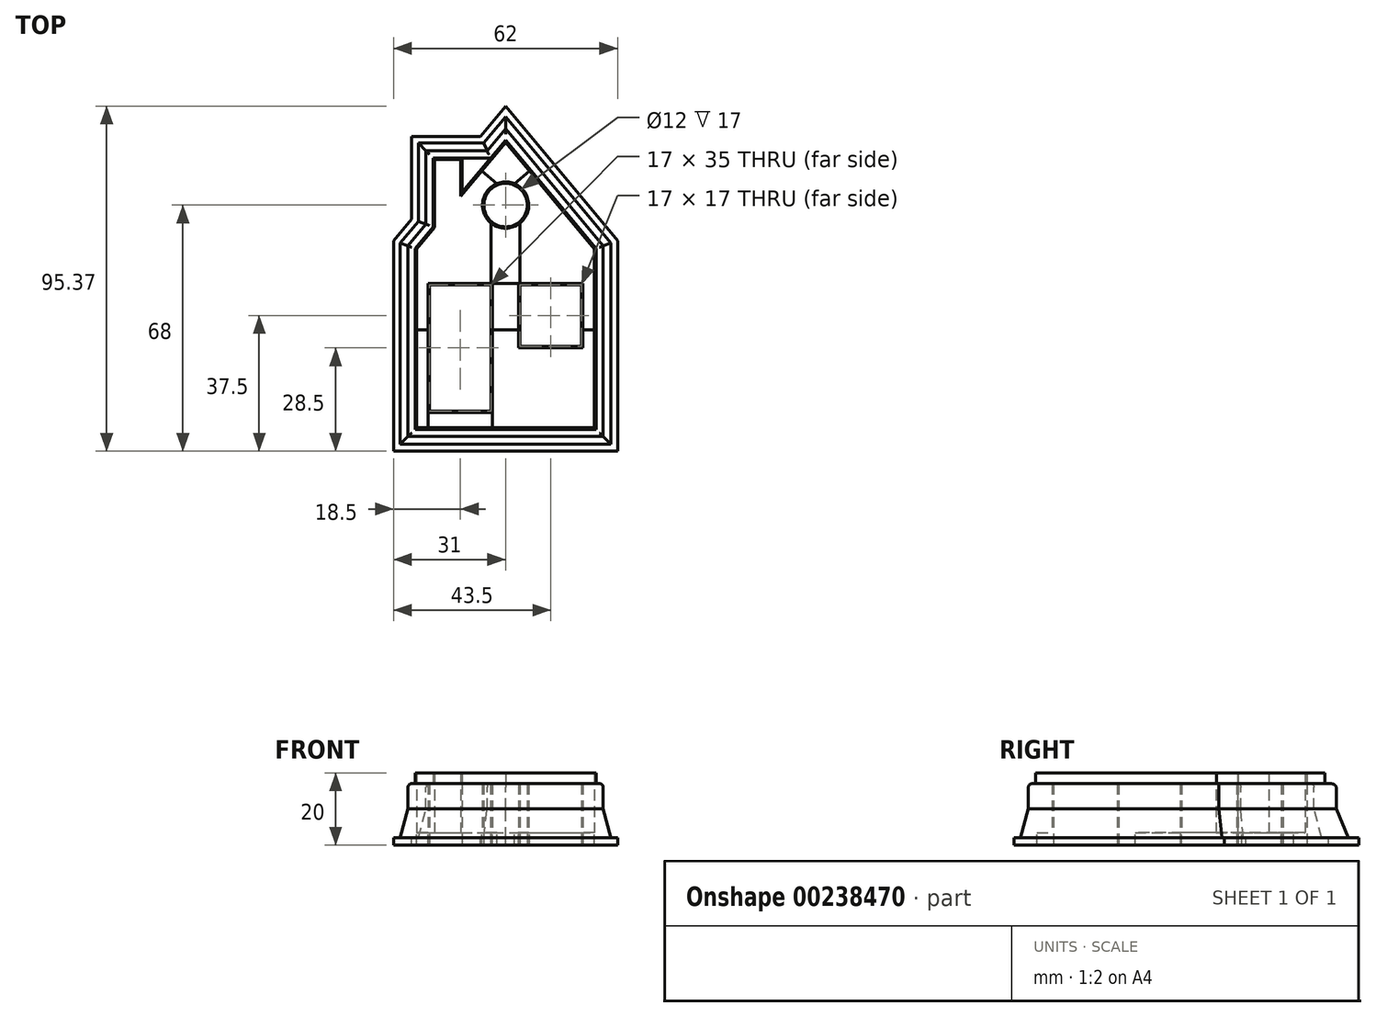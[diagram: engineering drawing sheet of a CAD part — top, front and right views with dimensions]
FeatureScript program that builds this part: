
annotation { "Feature Type Name" : "Feature", "Feature Type Description" : "" }
export const myFeature = defineFeature(function(context is Context, id is Id, definition is map)
    precondition{}
    {
        {
            var Q0;
            Q0=qCreatedBy(makeId("Top.planeOp"),FACE);
            var sketch = newSketch(context, id + "F0", { "sketchPlane" : qUnion([Q0])});
            skLineSegment(sketch, "E0.bottom", {"start": v(-25, 50) * mm, "end": v(25, 50) * mm});
            skLineSegment(sketch, "E0.top", {"start": v(-25, 0) * mm, "end": v(25, 0) * mm});
            skLineSegment(sketch, "E0.left", {"start": v(-25, 50) * mm, "end": v(-25, 0) * mm});
            skLineSegment(sketch, "E0.right", {"start": v(25, 50) * mm, "end": v(25, 0) * mm});
            skPoint(sketch, "E0.middle", {"position": v(0, 25) * mm});
            skLineSegment(sketch, "E1", {"start": v(-25, 50) * mm, "end": v(-20, 56) * mm});
            skLineSegment(sketch, "E2", {"start": v(0, 80) * mm, "end": v(25, 50) * mm});
            skLineSegment(sketch, "E3.bottom", {"start": v(-21, 5) * mm, "end": v(-4, 5) * mm});
            skLineSegment(sketch, "E3.top", {"start": v(-21, 40) * mm, "end": v(-4, 40) * mm});
            skLineSegment(sketch, "E3.left", {"start": v(-21, 5) * mm, "end": v(-21, 40) * mm});
            skLineSegment(sketch, "E3.right", {"start": v(-4, 5) * mm, "end": v(-4, 40) * mm});
            skLineSegment(sketch, "E4.bottom", {"start": v(4, 40) * mm, "end": v(21, 40) * mm});
            skLineSegment(sketch, "E4.top", {"start": v(4, 23) * mm, "end": v(21, 23) * mm});
            skLineSegment(sketch, "E4.left", {"start": v(4, 40) * mm, "end": v(4, 23) * mm});
            skLineSegment(sketch, "E4.right", {"start": v(21, 40) * mm, "end": v(21, 23) * mm});
            skLineSegment(sketch, "E5", {"start": v(-25, 40) * mm, "end": v(25, 40) * mm, "construction": true});
            skCircle(sketch, "E6", {"center": v(0, 62) * mm, "radius": 6 * mm});
            skLineSegment(sketch, "E7", {"start": v(-20, 56) * mm, "end": v(-20, 75) * mm});
            skLineSegment(sketch, "E8", {"start": v(-20, 75) * mm, "end": v(-12, 75) * mm});
            skLineSegment(sketch, "E9", {"start": v(-12, 75) * mm, "end": v(-12, 65.6) * mm});
            skLineSegment(sketch, "E10.trimOffspring", {"start": v(-12, 65.6) * mm, "end": v(0, 80) * mm});
            skSolve(sketch);
        }
        {
            var Q0;
            Q0=makeQuery(id+"F0.imprint","IMPRINT",FACE,{"disambiguationData":[TD([[makeQuery(id+"F0.imprint","IMPRINT",EDGE,{"derivedFrom":sQuery(id+"F0.wireOp",EDGE,"E0.bottom")}),1.0]])]});
            var Q1;
            Q1=makeQuery(id+"F0.imprint","IMPRINT",FACE,{"disambiguationData":[TD([[makeQuery(id+"F0.imprint","IMPRINT",EDGE,{"derivedFrom":sQuery(id+"F0.wireOp",EDGE,"E0.bottom")}),-1.0]])]});
            extrude(context, id + "F1", {"entities" : qUnion([Q0, Q1]), "depth" : 20 * mm});
        }
        {
            var Q0;
            Q0=makeQuery(id+"F1.opExtrude","CAP_FACE",FACE,{"disambiguationData":[OSD([sQuery(id+"F0.wireOp",EDGE,"E0.top"),sQuery(id+"F0.wireOp",EDGE,"E0.left"),sQuery(id+"F0.wireOp",EDGE,"E0.right"),sQuery(id+"F0.wireOp",EDGE,"E1"),sQuery(id+"F0.wireOp",EDGE,"E2"),sQuery(id+"F0.wireOp",EDGE,"E3.bottom"),sQuery(id+"F0.wireOp",EDGE,"E3.top"),sQuery(id+"F0.wireOp",EDGE,"E3.left"),sQuery(id+"F0.wireOp",EDGE,"E3.right"),sQuery(id+"F0.wireOp",EDGE,"E4.bottom"),sQuery(id+"F0.wireOp",EDGE,"E4.top"),sQuery(id+"F0.wireOp",EDGE,"E4.left"),sQuery(id+"F0.wireOp",EDGE,"E4.right"),sQuery(id+"F0.wireOp",EDGE,"E6"),sQuery(id+"F0.wireOp",EDGE,"E7"),sQuery(id+"F0.wireOp",EDGE,"E8"),sQuery(id+"F0.wireOp",EDGE,"E9"),sQuery(id+"F0.wireOp",EDGE,"E10.trimOffspring")])],"isStart":false});
            shell(context, id + "F2", {"entities" : qUnion([Q0]), "thickness" : 0.4 * mm});
        }
        {
            var Q0;
            {var subQ0=sQuery(id+"F0.wireOp",EDGE,"E10.trimOffspring");var subQ1=sQuery(id+"F0.wireOp",EDGE,"E9");var subQ2=sQuery(id+"F0.wireOp",EDGE,"E8");var subQ3=sQuery(id+"F0.wireOp",EDGE,"E7");var subQ4=sQuery(id+"F0.wireOp",EDGE,"E6");var subQ5=sQuery(id+"F0.wireOp",EDGE,"E4.right");var subQ6=sQuery(id+"F0.wireOp",EDGE,"E4.left");var subQ7=sQuery(id+"F0.wireOp",EDGE,"E4.top");var subQ8=sQuery(id+"F0.wireOp",EDGE,"E4.bottom");var subQ9=sQuery(id+"F0.wireOp",EDGE,"E3.right");var subQ10=sQuery(id+"F0.wireOp",EDGE,"E3.left");var subQ11=sQuery(id+"F0.wireOp",EDGE,"E3.top");var subQ12=sQuery(id+"F0.wireOp",EDGE,"E3.bottom");var subQ13=sQuery(id+"F0.wireOp",EDGE,"E2");var subQ14=sQuery(id+"F0.wireOp",EDGE,"E1");var subQ15=sQuery(id+"F0.wireOp",EDGE,"E0.right");var subQ16=sQuery(id+"F0.wireOp",EDGE,"E0.left");var subQ17=sQuery(id+"F0.wireOp",EDGE,"E0.top");Q0=makeQuery(id+"F2.opShell","OFFSET_FACE",FACE,{"disambiguationData":[OSD([subQ17,subQ16,subQ15,subQ14,subQ13,subQ12,subQ11,subQ10,subQ9,subQ8,subQ7,subQ6,subQ5,subQ4,subQ3,subQ2,subQ1,subQ0]),TDD([makeQuery(id+"F1.opExtrude","CAP_FACE",FACE,{"disambiguationData":[OSD([subQ17,subQ16,subQ15,subQ14,subQ13,subQ12,subQ11,subQ10,subQ9,subQ8,subQ7,subQ6,subQ5,subQ4,subQ3,subQ2,subQ1,subQ0])],"isStart":false})]),OD(2.0)]});}
            var Q1;
            Q1=makeQuery(id+"F1.opExtrude","CAP_FACE",FACE,{"disambiguationData":[OSD([sQuery(id+"F0.wireOp",EDGE,"E0.top"),sQuery(id+"F0.wireOp",EDGE,"E0.left"),sQuery(id+"F0.wireOp",EDGE,"E0.right"),sQuery(id+"F0.wireOp",EDGE,"E1"),sQuery(id+"F0.wireOp",EDGE,"E2"),sQuery(id+"F0.wireOp",EDGE,"E3.bottom"),sQuery(id+"F0.wireOp",EDGE,"E3.top"),sQuery(id+"F0.wireOp",EDGE,"E3.left"),sQuery(id+"F0.wireOp",EDGE,"E3.right"),sQuery(id+"F0.wireOp",EDGE,"E4.bottom"),sQuery(id+"F0.wireOp",EDGE,"E4.top"),sQuery(id+"F0.wireOp",EDGE,"E4.left"),sQuery(id+"F0.wireOp",EDGE,"E4.right"),sQuery(id+"F0.wireOp",EDGE,"E6"),sQuery(id+"F0.wireOp",EDGE,"E7"),sQuery(id+"F0.wireOp",EDGE,"E8"),sQuery(id+"F0.wireOp",EDGE,"E9"),sQuery(id+"F0.wireOp",EDGE,"E10.trimOffspring")])],"isStart":false});
            var Q2;
            {var subQ0=sQuery(id+"F0.wireOp",EDGE,"E10.trimOffspring");var subQ1=sQuery(id+"F0.wireOp",EDGE,"E9");var subQ2=sQuery(id+"F0.wireOp",EDGE,"E8");var subQ3=sQuery(id+"F0.wireOp",EDGE,"E7");var subQ4=sQuery(id+"F0.wireOp",EDGE,"E6");var subQ5=sQuery(id+"F0.wireOp",EDGE,"E4.right");var subQ6=sQuery(id+"F0.wireOp",EDGE,"E4.left");var subQ7=sQuery(id+"F0.wireOp",EDGE,"E4.top");var subQ8=sQuery(id+"F0.wireOp",EDGE,"E4.bottom");var subQ9=sQuery(id+"F0.wireOp",EDGE,"E3.right");var subQ10=sQuery(id+"F0.wireOp",EDGE,"E3.left");var subQ11=sQuery(id+"F0.wireOp",EDGE,"E3.top");var subQ12=sQuery(id+"F0.wireOp",EDGE,"E3.bottom");var subQ13=sQuery(id+"F0.wireOp",EDGE,"E2");var subQ14=sQuery(id+"F0.wireOp",EDGE,"E1");var subQ15=sQuery(id+"F0.wireOp",EDGE,"E0.right");var subQ16=sQuery(id+"F0.wireOp",EDGE,"E0.left");var subQ17=sQuery(id+"F0.wireOp",EDGE,"E0.top");Q2=makeQuery(id+"F2.opShell","OFFSET_FACE",FACE,{"disambiguationData":[OSD([subQ17,subQ16,subQ15,subQ14,subQ13,subQ12,subQ11,subQ10,subQ9,subQ8,subQ7,subQ6,subQ5,subQ4,subQ3,subQ2,subQ1,subQ0]),TDD([makeQuery(id+"F1.opExtrude","CAP_FACE",FACE,{"disambiguationData":[OSD([subQ17,subQ16,subQ15,subQ14,subQ13,subQ12,subQ11,subQ10,subQ9,subQ8,subQ7,subQ6,subQ5,subQ4,subQ3,subQ2,subQ1,subQ0])],"isStart":false})]),OD(1.0)]});}
            extrude(context, id + "F3", {"entities" : qUnion([Q0, Q1, Q2]), "operationType" : NewBodyOperationType.REMOVE, "oppositeDirection" : true, "depth" : 3 * mm});
        }
        {
            var Q0;
            {var subQ0=sQuery(id+"F0.wireOp",EDGE,"E10.trimOffspring");var subQ1=sQuery(id+"F0.wireOp",EDGE,"E9");var subQ2=sQuery(id+"F0.wireOp",EDGE,"E8");var subQ3=sQuery(id+"F0.wireOp",EDGE,"E7");var subQ4=sQuery(id+"F0.wireOp",EDGE,"E6");var subQ5=sQuery(id+"F0.wireOp",EDGE,"E4.right");var subQ6=sQuery(id+"F0.wireOp",EDGE,"E4.left");var subQ7=sQuery(id+"F0.wireOp",EDGE,"E4.top");var subQ8=sQuery(id+"F0.wireOp",EDGE,"E4.bottom");var subQ9=sQuery(id+"F0.wireOp",EDGE,"E3.right");var subQ10=sQuery(id+"F0.wireOp",EDGE,"E3.left");var subQ11=sQuery(id+"F0.wireOp",EDGE,"E3.top");var subQ12=sQuery(id+"F0.wireOp",EDGE,"E3.bottom");var subQ13=sQuery(id+"F0.wireOp",EDGE,"E2");var subQ14=sQuery(id+"F0.wireOp",EDGE,"E1");var subQ15=sQuery(id+"F0.wireOp",EDGE,"E0.right");var subQ16=sQuery(id+"F0.wireOp",EDGE,"E0.left");var subQ17=sQuery(id+"F0.wireOp",EDGE,"E0.top");Q0=makeQuery(id+"F2.opShell","OFFSET_FACE",FACE,{"disambiguationData":[OSD([subQ17,subQ16,subQ15,subQ14,subQ13,subQ12,subQ11,subQ10,subQ9,subQ8,subQ7,subQ6,subQ5,subQ4,subQ3,subQ2,subQ1,subQ0]),TDD([makeQuery(id+"F1.opExtrude","CAP_FACE",FACE,{"disambiguationData":[OSD([subQ17,subQ16,subQ15,subQ14,subQ13,subQ12,subQ11,subQ10,subQ9,subQ8,subQ7,subQ6,subQ5,subQ4,subQ3,subQ2,subQ1,subQ0])],"isStart":true})])]});}
            var sketch = newSketch(context, id + "F4", { "sketchPlane" : qUnion([Q0])});
            skLineSegment(sketch, "E11.0", {"start": v(3.6, 22.6) * mm, "end": v(21.4, 22.6) * mm});
            skLineSegment(sketch, "E11.1", {"start": v(21.4, 40.4) * mm, "end": v(21.4, 22.6) * mm});
            skLineSegment(sketch, "E11.2", {"start": v(3.6, 40.4) * mm, "end": v(21.4, 40.4) * mm});
            skLineSegment(sketch, "E11.3", {"start": v(3.6, 40.4) * mm, "end": v(3.6, 22.6) * mm});
            skLineSegment(sketch, "E12.0", {"start": v(-3.6, 4.6) * mm, "end": v(-3.6, 40.4) * mm});
            skLineSegment(sketch, "E12.1", {"start": v(-21.4, 4.6) * mm, "end": v(-3.6, 4.6) * mm});
            skLineSegment(sketch, "E12.2", {"start": v(-21.4, 4.6) * mm, "end": v(-21.4, 40.4) * mm});
            skLineSegment(sketch, "E12.3", {"start": v(-21.4, 40.4) * mm, "end": v(-3.6, 40.4) * mm});
            skLineSegment(sketch, "E13.0", {"start": v(0, 79.38) * mm, "end": v(24.6, 49.86) * mm});
            skLineSegment(sketch, "E14.0", {"start": v(24.6, 49.86) * mm, "end": v(24.6, 0.4) * mm});
            skLineSegment(sketch, "E15.0", {"start": v(-12.4, 64.5) * mm, "end": v(0, 79.38) * mm});
            skCircle(sketch, "E16.0", {"center": v(0, 62) * mm, "radius": 6.4 * mm});
            skLineSegment(sketch, "E17.0", {"start": v(-12.4, 74.6) * mm, "end": v(-12.4, 64.5) * mm});
            skLineSegment(sketch, "E17.1", {"start": v(-19.6, 74.6) * mm, "end": v(-12.4, 74.6) * mm});
            skLineSegment(sketch, "E17.2", {"start": v(-19.6, 55.86) * mm, "end": v(-19.6, 74.6) * mm});
            skLineSegment(sketch, "E17.3", {"start": v(-24.6, 49.86) * mm, "end": v(-19.6, 55.86) * mm});
            skLineSegment(sketch, "E17.4", {"start": v(-24.6, 49.86) * mm, "end": v(-24.6, 0.4) * mm});
            skLineSegment(sketch, "E17.5", {"start": v(-24.6, 0.4) * mm, "end": v(24.6, 0.4) * mm});
            skLineSegment(sketch, "E18", {"start": v(-3.6, 33.81) * mm, "end": v(3.6, 33.81) * mm});
            skLineSegment(sketch, "E19", {"start": v(21.4, 33.81) * mm, "end": v(24.6, 33.81) * mm});
            skLineSegment(sketch, "E20", {"start": v(24.6, 27.52) * mm, "end": v(21.4, 27.52) * mm});
            skLineSegment(sketch, "E21", {"start": v(3.6, 27.52) * mm, "end": v(-3.6, 27.52) * mm});
            skLineSegment(sketch, "E22", {"start": v(-21.4, 27.52) * mm, "end": v(-24.6, 27.52) * mm});
            skLineSegment(sketch, "E23", {"start": v(-21.4, 33.81) * mm, "end": v(-24.6, 33.81) * mm});
            skLineSegment(sketch, "E24", {"start": v(-10.47, 66.82) * mm, "end": v(-6.26, 63.31) * mm});
            skLineSegment(sketch, "E25", {"start": v(-2.42, 67.92) * mm, "end": v(-6.62, 71.43) * mm});
            skLineSegment(sketch, "E26", {"start": v(2.42, 67.92) * mm, "end": v(6.62, 71.43) * mm});
            skLineSegment(sketch, "E27", {"start": v(10.47, 66.82) * mm, "end": v(6.26, 63.31) * mm});
            skLineSegment(sketch, "E28", {"start": v(0, 62) * mm, "end": v(8.55, 69.12) * mm, "construction": true});
            skLineSegment(sketch, "E29", {"start": v(0, 62) * mm, "end": v(-8.55, 69.12) * mm, "construction": true});
            skLineSegment(sketch, "E30", {"start": v(-4, 57) * mm, "end": v(-4, 40.4) * mm});
            skLineSegment(sketch, "E31", {"start": v(-4, 40.4) * mm, "end": v(4, 40.4) * mm});
            skLineSegment(sketch, "E32", {"start": v(4, 40.4) * mm, "end": v(4, 57) * mm});
            skLineSegment(sketch, "E33", {"start": v(0, 62) * mm, "end": v(0, 40.4) * mm, "construction": true});
            skLineSegment(sketch, "E34", {"start": v(-3.6, 4.6) * mm, "end": v(-3.6, 0.4) * mm});
            skLineSegment(sketch, "E35", {"start": v(-21.4, 4.6) * mm, "end": v(-21.4, 0.4) * mm});
            skSolve(sketch);
        }
        {
            var Q0;
            {var subQ0=sQuery(id+"F4.wireOp",EDGE,"E25");Q0=makeQuery(id+"F4.imprint","IMPRINT",FACE,{"disambiguationData":[TD([[makeQuery(id+"F4.imprint","IMPRINT",EDGE,{"derivedFrom":subQ0}),-1.0]])]});}
            var Q1;
            {var subQ1=sQuery(id+"F4.wireOp",EDGE,"E12.3");Q1=makeQuery(id+"F4.imprint","IMPRINT",FACE,{"disambiguationData":[TD([[makeQuery(id+"F4.imprint","IMPRINT",EDGE,{"derivedFrom":subQ1}),1.0]])]});}
            var Q2;
            {var subQ4=sQuery(id+"F4.wireOp",EDGE,"E11.2");Q2=makeQuery(id+"F4.imprint","IMPRINT",FACE,{"disambiguationData":[TD([[makeQuery(id+"F4.imprint","IMPRINT",EDGE,{"derivedFrom":subQ4}),1.0]])]});}
            var Q3;
            {var subQ9=sQuery(id+"F4.wireOp",EDGE,"E11.0");Q3=makeQuery(id+"F4.imprint","IMPRINT",FACE,{"disambiguationData":[TD([[makeQuery(id+"F4.imprint","IMPRINT",EDGE,{"derivedFrom":subQ9}),-1.0]])]});}
            var Q4;
            {var subQ4=sQuery(id+"F4.wireOp",EDGE,"E22");Q4=makeQuery(id+"F4.imprint","IMPRINT",FACE,{"disambiguationData":[TD([[makeQuery(id+"F4.imprint","IMPRINT",EDGE,{"derivedFrom":subQ4}),1.0]])]});}
            extrude(context, id + "F5", {"entities" : qUnion([Q0, Q1, Q2, Q3, Q4]), "operationType" : NewBodyOperationType.REMOVE, "endBound" : BoundingType.UP_TO_NEXT, "oppositeDirection" : true, "depth" : 25 * mm});
        }
        {
            var Q0;
            {var subQ3=sQuery(id+"F0.wireOp",EDGE,"E6");var subQ4=sQuery(id+"F0.wireOp",EDGE,"E3.top");var subQ5=sQuery(id+"F0.wireOp",EDGE,"E3.right");var subQ6=sQuery(id+"F0.wireOp",EDGE,"E4.bottom");var subQ7=sQuery(id+"F0.wireOp",EDGE,"E4.left");var subQ8=sQuery(id+"F0.wireOp",EDGE,"E10.trimOffspring");var subQ9=sQuery(id+"F0.wireOp",EDGE,"E9");var subQ10=sQuery(id+"F0.wireOp",EDGE,"E8");var subQ11=sQuery(id+"F0.wireOp",EDGE,"E7");var subQ12=sQuery(id+"F0.wireOp",EDGE,"E4.right");var subQ13=sQuery(id+"F0.wireOp",EDGE,"E4.top");var subQ14=sQuery(id+"F0.wireOp",EDGE,"E3.left");var subQ15=sQuery(id+"F0.wireOp",EDGE,"E3.bottom");var subQ16=sQuery(id+"F0.wireOp",EDGE,"E2");var subQ17=sQuery(id+"F0.wireOp",EDGE,"E1");var subQ18=sQuery(id+"F0.wireOp",EDGE,"E0.right");var subQ19=sQuery(id+"F0.wireOp",EDGE,"E0.left");var subQ20=sQuery(id+"F0.wireOp",EDGE,"E0.top");Q0=makeQuery(id+"F5.boolean.opBoolean","SPLIT",FACE,{"disambiguationData":[TD([makeQuery(id+"F2.opShell","OFFSET_FACE",FACE,{"disambiguationData":[OSD([subQ4])]})])],"derivedFrom":makeQuery(id+"F2.opShell","OFFSET_FACE",FACE,{"disambiguationData":[OSD([subQ20,subQ19,subQ18,subQ17,subQ16,subQ15,subQ4,subQ14,subQ5,subQ6,subQ13,subQ7,subQ12,subQ3,subQ11,subQ10,subQ9,subQ8]),TDD([makeQuery(id+"F1.opExtrude","CAP_FACE",FACE,{"disambiguationData":[OSD([subQ20,subQ19,subQ18,subQ17,subQ16,subQ15,subQ4,subQ14,subQ5,subQ6,subQ13,subQ7,subQ12,subQ3,subQ11,subQ10,subQ9,subQ8])],"isStart":true})])]})});}
            var Q1;
            {var subQ2=sQuery(id+"F0.wireOp",EDGE,"E6");var subQ3=sQuery(id+"F0.wireOp",EDGE,"E10.trimOffspring");var subQ6=sQuery(id+"F0.wireOp",EDGE,"E9");var subQ7=sQuery(id+"F0.wireOp",EDGE,"E8");var subQ8=sQuery(id+"F0.wireOp",EDGE,"E7");var subQ9=sQuery(id+"F0.wireOp",EDGE,"E4.right");var subQ10=sQuery(id+"F0.wireOp",EDGE,"E4.left");var subQ11=sQuery(id+"F0.wireOp",EDGE,"E4.top");var subQ12=sQuery(id+"F0.wireOp",EDGE,"E4.bottom");var subQ13=sQuery(id+"F0.wireOp",EDGE,"E3.right");var subQ14=sQuery(id+"F0.wireOp",EDGE,"E3.left");var subQ15=sQuery(id+"F0.wireOp",EDGE,"E3.top");var subQ16=sQuery(id+"F0.wireOp",EDGE,"E3.bottom");var subQ17=sQuery(id+"F0.wireOp",EDGE,"E2");var subQ18=sQuery(id+"F0.wireOp",EDGE,"E1");var subQ19=sQuery(id+"F0.wireOp",EDGE,"E0.right");var subQ20=sQuery(id+"F0.wireOp",EDGE,"E0.left");var subQ21=sQuery(id+"F0.wireOp",EDGE,"E0.top");Q1=makeQuery(id+"F5.boolean.opBoolean","SPLIT",FACE,{"disambiguationData":[TD([makeQuery(id+"F2.opShell","OFFSET_FACE",FACE,{"disambiguationData":[OSD([subQ3])]})])],"derivedFrom":makeQuery(id+"F2.opShell","OFFSET_FACE",FACE,{"disambiguationData":[OSD([subQ21,subQ20,subQ19,subQ18,subQ17,subQ16,subQ15,subQ14,subQ13,subQ12,subQ11,subQ10,subQ9,subQ2,subQ8,subQ7,subQ6,subQ3]),TDD([makeQuery(id+"F1.opExtrude","CAP_FACE",FACE,{"disambiguationData":[OSD([subQ21,subQ20,subQ19,subQ18,subQ17,subQ16,subQ15,subQ14,subQ13,subQ12,subQ11,subQ10,subQ9,subQ2,subQ8,subQ7,subQ6,subQ3])],"isStart":true})])]})});}
            var Q2;
            {var subQ4=sQuery(id+"F0.wireOp",EDGE,"E6");var subQ5=sQuery(id+"F0.wireOp",EDGE,"E2");var subQ6=sQuery(id+"F0.wireOp",EDGE,"E10.trimOffspring");var subQ7=sQuery(id+"F0.wireOp",EDGE,"E9");var subQ8=sQuery(id+"F0.wireOp",EDGE,"E8");var subQ9=sQuery(id+"F0.wireOp",EDGE,"E7");var subQ10=sQuery(id+"F0.wireOp",EDGE,"E4.right");var subQ11=sQuery(id+"F0.wireOp",EDGE,"E4.left");var subQ12=sQuery(id+"F0.wireOp",EDGE,"E4.top");var subQ13=sQuery(id+"F0.wireOp",EDGE,"E4.bottom");var subQ14=sQuery(id+"F0.wireOp",EDGE,"E3.right");var subQ15=sQuery(id+"F0.wireOp",EDGE,"E3.left");var subQ16=sQuery(id+"F0.wireOp",EDGE,"E3.top");var subQ17=sQuery(id+"F0.wireOp",EDGE,"E3.bottom");var subQ18=sQuery(id+"F0.wireOp",EDGE,"E1");var subQ19=sQuery(id+"F0.wireOp",EDGE,"E0.right");var subQ20=sQuery(id+"F0.wireOp",EDGE,"E0.left");var subQ21=sQuery(id+"F0.wireOp",EDGE,"E0.top");Q2=makeQuery(id+"F5.boolean.opBoolean","SPLIT",FACE,{"disambiguationData":[TD([makeQuery(id+"F2.opShell","OFFSET_FACE",FACE,{"disambiguationData":[OSD([subQ5])]})])],"derivedFrom":makeQuery(id+"F2.opShell","OFFSET_FACE",FACE,{"disambiguationData":[OSD([subQ21,subQ20,subQ19,subQ18,subQ5,subQ17,subQ16,subQ15,subQ14,subQ13,subQ12,subQ11,subQ10,subQ4,subQ9,subQ8,subQ7,subQ6]),TDD([makeQuery(id+"F1.opExtrude","CAP_FACE",FACE,{"disambiguationData":[OSD([subQ21,subQ20,subQ19,subQ18,subQ5,subQ17,subQ16,subQ15,subQ14,subQ13,subQ12,subQ11,subQ10,subQ4,subQ9,subQ8,subQ7,subQ6])],"isStart":true})])]})});}
            var Q3;
            {var subQ4=sQuery(id+"F0.wireOp",EDGE,"E4.right");var subQ5=sQuery(id+"F0.wireOp",EDGE,"E0.right");var subQ6=sQuery(id+"F0.wireOp",EDGE,"E10.trimOffspring");var subQ7=sQuery(id+"F0.wireOp",EDGE,"E9");var subQ8=sQuery(id+"F0.wireOp",EDGE,"E8");var subQ9=sQuery(id+"F0.wireOp",EDGE,"E7");var subQ10=sQuery(id+"F0.wireOp",EDGE,"E6");var subQ11=sQuery(id+"F0.wireOp",EDGE,"E4.left");var subQ12=sQuery(id+"F0.wireOp",EDGE,"E4.top");var subQ13=sQuery(id+"F0.wireOp",EDGE,"E4.bottom");var subQ14=sQuery(id+"F0.wireOp",EDGE,"E3.right");var subQ15=sQuery(id+"F0.wireOp",EDGE,"E3.left");var subQ16=sQuery(id+"F0.wireOp",EDGE,"E3.top");var subQ17=sQuery(id+"F0.wireOp",EDGE,"E3.bottom");var subQ18=sQuery(id+"F0.wireOp",EDGE,"E2");var subQ19=sQuery(id+"F0.wireOp",EDGE,"E1");var subQ20=sQuery(id+"F0.wireOp",EDGE,"E0.left");var subQ21=sQuery(id+"F0.wireOp",EDGE,"E0.top");Q3=makeQuery(id+"F5.boolean.opBoolean","SPLIT",FACE,{"disambiguationData":[TD([makeQuery(id+"F2.opShell","OFFSET_FACE",FACE,{"disambiguationData":[OSD([subQ5])]})])],"derivedFrom":makeQuery(id+"F2.opShell","OFFSET_FACE",FACE,{"disambiguationData":[OSD([subQ21,subQ20,subQ5,subQ19,subQ18,subQ17,subQ16,subQ15,subQ14,subQ13,subQ12,subQ11,subQ4,subQ10,subQ9,subQ8,subQ7,subQ6]),TDD([makeQuery(id+"F1.opExtrude","CAP_FACE",FACE,{"disambiguationData":[OSD([subQ21,subQ20,subQ5,subQ19,subQ18,subQ17,subQ16,subQ15,subQ14,subQ13,subQ12,subQ11,subQ4,subQ10,subQ9,subQ8,subQ7,subQ6])],"isStart":true})])]})});}
            var Q4;
            {var subQ2=sQuery(id+"F0.wireOp",EDGE,"E3.left");var subQ4=sQuery(id+"F0.wireOp",EDGE,"E0.left");var subQ6=sQuery(id+"F0.wireOp",EDGE,"E10.trimOffspring");var subQ7=sQuery(id+"F0.wireOp",EDGE,"E9");var subQ8=sQuery(id+"F0.wireOp",EDGE,"E8");var subQ9=sQuery(id+"F0.wireOp",EDGE,"E7");var subQ10=sQuery(id+"F0.wireOp",EDGE,"E6");var subQ11=sQuery(id+"F0.wireOp",EDGE,"E4.right");var subQ12=sQuery(id+"F0.wireOp",EDGE,"E4.left");var subQ13=sQuery(id+"F0.wireOp",EDGE,"E4.top");var subQ14=sQuery(id+"F0.wireOp",EDGE,"E4.bottom");var subQ15=sQuery(id+"F0.wireOp",EDGE,"E3.right");var subQ16=sQuery(id+"F0.wireOp",EDGE,"E3.top");var subQ17=sQuery(id+"F0.wireOp",EDGE,"E3.bottom");var subQ18=sQuery(id+"F0.wireOp",EDGE,"E2");var subQ19=sQuery(id+"F0.wireOp",EDGE,"E1");var subQ20=sQuery(id+"F0.wireOp",EDGE,"E0.right");var subQ21=sQuery(id+"F0.wireOp",EDGE,"E0.top");Q4=makeQuery(id+"F5.boolean.opBoolean","SPLIT",FACE,{"disambiguationData":[TD([makeQuery(id+"F2.opShell","OFFSET_FACE",FACE,{"disambiguationData":[OSD([subQ4])]})])],"derivedFrom":makeQuery(id+"F2.opShell","OFFSET_FACE",FACE,{"disambiguationData":[OSD([subQ21,subQ4,subQ20,subQ19,subQ18,subQ17,subQ16,subQ2,subQ15,subQ14,subQ13,subQ12,subQ11,subQ10,subQ9,subQ8,subQ7,subQ6]),TDD([makeQuery(id+"F1.opExtrude","CAP_FACE",FACE,{"disambiguationData":[OSD([subQ21,subQ4,subQ20,subQ19,subQ18,subQ17,subQ16,subQ2,subQ15,subQ14,subQ13,subQ12,subQ11,subQ10,subQ9,subQ8,subQ7,subQ6])],"isStart":true})])]})});}
            var Q5;
            {var subQ0=sQuery(id+"F0.wireOp",EDGE,"E3.right");var subQ2=sQuery(id+"F0.wireOp",EDGE,"E3.left");var subQ3=sQuery(id+"F0.wireOp",EDGE,"E3.bottom");var subQ4=sQuery(id+"F0.wireOp",EDGE,"E0.top");var subQ8=sQuery(id+"F0.wireOp",EDGE,"E10.trimOffspring");var subQ9=sQuery(id+"F0.wireOp",EDGE,"E9");var subQ10=sQuery(id+"F0.wireOp",EDGE,"E8");var subQ11=sQuery(id+"F0.wireOp",EDGE,"E7");var subQ12=sQuery(id+"F0.wireOp",EDGE,"E6");var subQ13=sQuery(id+"F0.wireOp",EDGE,"E4.right");var subQ14=sQuery(id+"F0.wireOp",EDGE,"E4.left");var subQ15=sQuery(id+"F0.wireOp",EDGE,"E4.top");var subQ16=sQuery(id+"F0.wireOp",EDGE,"E4.bottom");var subQ17=sQuery(id+"F0.wireOp",EDGE,"E3.top");var subQ18=sQuery(id+"F0.wireOp",EDGE,"E2");var subQ19=sQuery(id+"F0.wireOp",EDGE,"E1");var subQ20=sQuery(id+"F0.wireOp",EDGE,"E0.right");var subQ21=sQuery(id+"F0.wireOp",EDGE,"E0.left");Q5=makeQuery(id+"F5.boolean.opBoolean","SPLIT",FACE,{"disambiguationData":[TD([makeQuery(id+"F2.opShell","OFFSET_FACE",FACE,{"disambiguationData":[OSD([subQ4])]})])],"derivedFrom":makeQuery(id+"F2.opShell","OFFSET_FACE",FACE,{"disambiguationData":[OSD([subQ4,subQ21,subQ20,subQ19,subQ18,subQ3,subQ17,subQ2,subQ0,subQ16,subQ15,subQ14,subQ13,subQ12,subQ11,subQ10,subQ9,subQ8]),TDD([makeQuery(id+"F1.opExtrude","CAP_FACE",FACE,{"disambiguationData":[OSD([subQ4,subQ21,subQ20,subQ19,subQ18,subQ3,subQ17,subQ2,subQ0,subQ16,subQ15,subQ14,subQ13,subQ12,subQ11,subQ10,subQ9,subQ8])],"isStart":true})])]})});}
            extrude(context, id + "F6", {"entities" : qUnion([Q0, Q1, Q2, Q3, Q4, Q5]), "operationType" : NewBodyOperationType.ADD, "depth" : 3 * mm});
        }
        {
            var Q0;
            {var subQ0=sQuery(id+"F0.wireOp",EDGE,"E10.trimOffspring");var subQ1=sQuery(id+"F0.wireOp",EDGE,"E9");var subQ2=sQuery(id+"F0.wireOp",EDGE,"E8");var subQ3=sQuery(id+"F0.wireOp",EDGE,"E7");var subQ4=sQuery(id+"F0.wireOp",EDGE,"E6");var subQ5=sQuery(id+"F0.wireOp",EDGE,"E4.right");var subQ6=sQuery(id+"F0.wireOp",EDGE,"E4.left");var subQ7=sQuery(id+"F0.wireOp",EDGE,"E4.top");var subQ8=sQuery(id+"F0.wireOp",EDGE,"E4.bottom");var subQ9=sQuery(id+"F0.wireOp",EDGE,"E3.right");var subQ10=sQuery(id+"F0.wireOp",EDGE,"E3.left");var subQ11=sQuery(id+"F0.wireOp",EDGE,"E3.top");var subQ12=sQuery(id+"F0.wireOp",EDGE,"E3.bottom");var subQ13=sQuery(id+"F0.wireOp",EDGE,"E2");var subQ14=sQuery(id+"F0.wireOp",EDGE,"E1");var subQ15=sQuery(id+"F0.wireOp",EDGE,"E0.right");var subQ16=sQuery(id+"F0.wireOp",EDGE,"E0.left");var subQ17=sQuery(id+"F0.wireOp",EDGE,"E0.top");Q0=makeQuery(id+"F2.opShell","OFFSET_FACE",FACE,{"disambiguationData":[OSD([subQ17,subQ16,subQ15,subQ14,subQ13,subQ12,subQ11,subQ10,subQ9,subQ8,subQ7,subQ6,subQ5,subQ4,subQ3,subQ2,subQ1,subQ0]),TDD([makeQuery(id+"F1.opExtrude","CAP_FACE",FACE,{"disambiguationData":[OSD([subQ17,subQ16,subQ15,subQ14,subQ13,subQ12,subQ11,subQ10,subQ9,subQ8,subQ7,subQ6,subQ5,subQ4,subQ3,subQ2,subQ1,subQ0])],"isStart":false})]),OD(0.0)]});}
            var sketch = newSketch(context, id + "F7", { "sketchPlane" : qUnion([Q0])});
            skLineSegment(sketch, "E36.0", {"start": v(25, 50) * mm, "end": v(25, 0) * mm});
            skLineSegment(sketch, "E37.0", {"start": v(-25, 0) * mm, "end": v(25, 0) * mm});
            skLineSegment(sketch, "E38.0", {"start": v(-25, 50) * mm, "end": v(-25, 0) * mm});
            skLineSegment(sketch, "E38.1", {"start": v(-25, 50) * mm, "end": v(-20, 56) * mm});
            skLineSegment(sketch, "E38.2", {"start": v(-20, 56) * mm, "end": v(-20, 75) * mm});
            skLineSegment(sketch, "E38.3", {"start": v(-20, 75) * mm, "end": v(-12, 75) * mm});
            skLineSegment(sketch, "E38.5", {"start": v(-4.17, 75) * mm, "end": v(0, 80) * mm});
            skLineSegment(sketch, "E38.6", {"start": v(0, 80) * mm, "end": v(25, 50) * mm});
            skLineSegment(sketch, "E39", {"start": v(-12, 75) * mm, "end": v(-4.17, 75) * mm});
            skPoint(sketch, "E40.orphan", {"position": v(-12, 65.6) * mm});
            skSolve(sketch);
        }
        {
            var Q0;
            Q0=qCreatedBy(makeId("Front.planeOp"),FACE);
            var sketch = newSketch(context, id + "F8", { "sketchPlane" : qUnion([Q0])});
            skLineSegment(sketch, "E41.0", {"start": v(25, 20) * mm, "end": v(25, 0) * mm});
            skLineSegment(sketch, "E42", {"start": v(25, 17) * mm, "end": v(26, 17) * mm});
            skLineSegment(sketch, "E43", {"start": v(27, 16) * mm, "end": v(27, 10) * mm});
            skLineSegment(sketch, "E44", {"start": v(27, 10) * mm, "end": v(29.14, 2) * mm});
            skLineSegment(sketch, "E45", {"start": v(29.14, 2) * mm, "end": v(31, 2) * mm});
            skLineSegment(sketch, "E46", {"start": v(31, 2) * mm, "end": v(31, 0) * mm});
            skLineSegment(sketch, "E47", {"start": v(31, 0) * mm, "end": v(25, 0) * mm});
            skPoint(sketch, "E48.visualSharp", {"position": v(27, 17) * mm});
            skArc(sketch, "E48.filletArc", {"start": v(27, 16) * mm, "mid": v(26.7, 16.7) * mm, "end": v(26, 17) * mm});
            skSolve(sketch);
        }
        {
            var Q0;
            {var subQ0=sQuery(id+"F8.wireOp",EDGE,"E42");Q0=makeQuery(id+"F8.imprint","IMPRINT",FACE,{"disambiguationData":[TD([[makeQuery(id+"F8.imprint","IMPRINT",EDGE,{"derivedFrom":subQ0}),-1.0]])]});}
            var Q1;
            Q1 = qConstructionFilter(qBodyType(qCreatedBy(id + "F7" ,EDGE), BodyType.WIRE), ConstructionObject.NO);
            sweep(context, id + "F9", {"operationType" : NewBodyOperationType.ADD, "profiles" : qUnion([Q0]), "path" : qUnion([Q1])});
        }
    });
